# Revit family: KLS - wall_furniture
name_source: partatom
category: Generic Models
revit_build: Autodesk Revit 2014 (Build: 20130308_1515(x64)
units: mm (PartAtom-declared; Revit-internal decimal feet)

## types (5) — shared parameters
Default Elevation = 1219 mm
hole = 30 mm  [stored 0.0984252 ft]
material = <By Category>
thickness around hole = 30 mm  [stored 0.0984252 ft]
wall thickness = 30 mm  [stored 0.0984252 ft]
width = 1000 mm  [stored 3.28084 ft]

## per-type parameters (varying)
| type | height |
| wooden wall_114cm | 1140 mm  [stored 3.74016 ft] |
| wooden wall_144cm | 1440 mm  [stored 4.72441 ft] |
| wooden wall_174cm | 1740 mm  [stored 5.70866 ft] |
| wooden wall_204cm | 2040 mm  [stored 6.69291 ft] |
| wooden wall_234cm | 2340 mm  [stored 7.67717 ft] |

note: [stored X ft] marks values corroborated as IEEE doubles in the binary element streams (Revit-internal decimal feet)

## geometry (parser evidence)
native form markers: Sweep x1
no freeform markers — native parametric forms only
